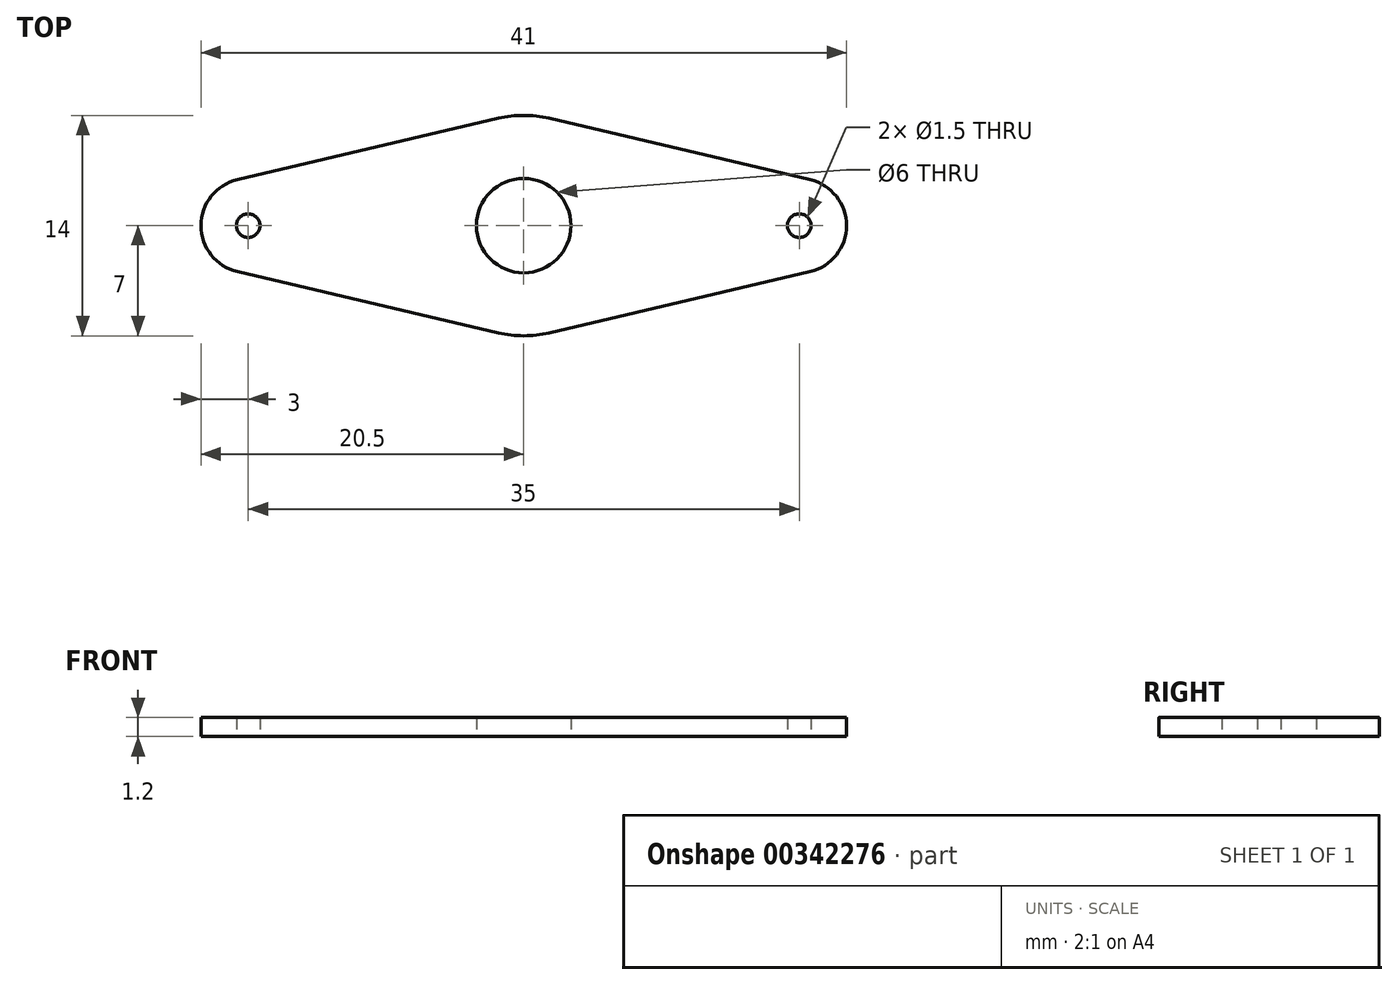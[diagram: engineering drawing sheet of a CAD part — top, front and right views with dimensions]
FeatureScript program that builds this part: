
annotation { "Feature Type Name" : "Feature", "Feature Type Description" : "" }
export const myFeature = defineFeature(function(context is Context, id is Id, definition is map)
    precondition{}
    {
        {
            var Q0;
            Q0=qCreatedBy(makeId("Top.planeOp"),FACE);
            var sketch = newSketch(context, id + "F0", { "sketchPlane" : qUnion([Q0])});
            skLineSegment(sketch, "E0", {"start": v(0, 0) * mm, "end": v(1.6, -6.81) * mm, "construction": true});
            skLineSegment(sketch, "E1", {"start": v(1.6, -6.81) * mm, "end": v(18.19, -2.92) * mm});
            skLineSegment(sketch, "E2", {"start": v(18.19, -2.92) * mm, "end": v(17.5, 0) * mm, "construction": true});
            skArc(sketch, "E3", {"start": v(1.6, -6.81) * mm, "mid": v(0.8, -6.95) * mm, "end": v(0, -7) * mm});
            skArc(sketch, "E4", {"start": v(18.19, -2.92) * mm, "mid": v(19.85, -1.86) * mm, "end": v(20.5, 0) * mm});
            skArc(sketch, "E5", {"start": v(16.75, 0) * mm, "mid": v(17.5, -0.75) * mm, "end": v(18.25, 0) * mm});
            skArc(sketch, "E6", {"start": v(3, 0) * mm, "mid": v(2.12, -2.12) * mm, "end": v(0, -3) * mm});
            skLineSegment(sketch, "E7", {"start": v(0, -7) * mm, "end": v(0, -3) * mm});
            skLineSegment(sketch, "E8", {"start": v(3, 0) * mm, "end": v(16.75, 0) * mm});
            skLineSegment(sketch, "E9", {"start": v(18.25, 0) * mm, "end": v(20.5, 0) * mm});
            skSolve(sketch);
        }
        {
            var Q0;
            Q0=makeQuery(id+"F0.imprint","IMPRINT",FACE,{"disambiguationData":[TD([[makeQuery(id+"F0.imprint","IMPRINT",EDGE,{"derivedFrom":sQuery(id+"F0.wireOp",EDGE,"E1")}),1.0]])]});
            extrude(context, id + "F1", {"entities" : qUnion([Q0]), "depth" : 1.2 * mm});
        }
        {
            var Q0;
            Q0=makeQuery(id+"F1.opExtrude","SWEPT_BODY",BODY,{"disambiguationData":[OSD([sQuery(id+"F0.wireOp",EDGE,"E1"),sQuery(id+"F0.wireOp",EDGE,"E3"),sQuery(id+"F0.wireOp",EDGE,"E4"),sQuery(id+"F0.wireOp",EDGE,"E5"),sQuery(id+"F0.wireOp",EDGE,"E6"),sQuery(id+"F0.wireOp",EDGE,"E7"),sQuery(id+"F0.wireOp",EDGE,"E8"),sQuery(id+"F0.wireOp",EDGE,"E9")])]});
            var Q1;
            Q1=qCreatedBy(makeId("Right.planeOp"),FACE);
            mirror(context, id + "F2", {"operationType" : NewBodyOperationType.ADD, "entities" : qUnion([Q0]), "mirrorPlane" : qUnion([Q1])});
        }
        {
            var Q0;
            Q0=makeQuery(id+"F1.opExtrude","SWEPT_BODY",BODY,{"disambiguationData":[OSD([sQuery(id+"F0.wireOp",EDGE,"E1"),sQuery(id+"F0.wireOp",EDGE,"E3"),sQuery(id+"F0.wireOp",EDGE,"E4"),sQuery(id+"F0.wireOp",EDGE,"E5"),sQuery(id+"F0.wireOp",EDGE,"E6"),sQuery(id+"F0.wireOp",EDGE,"E7"),sQuery(id+"F0.wireOp",EDGE,"E8"),sQuery(id+"F0.wireOp",EDGE,"E9")])]});
            var Q1;
            Q1=qCreatedBy(makeId("Front.planeOp"),FACE);
            mirror(context, id + "F3", {"operationType" : NewBodyOperationType.ADD, "entities" : qUnion([Q0]), "mirrorPlane" : qUnion([Q1])});
        }
    });
